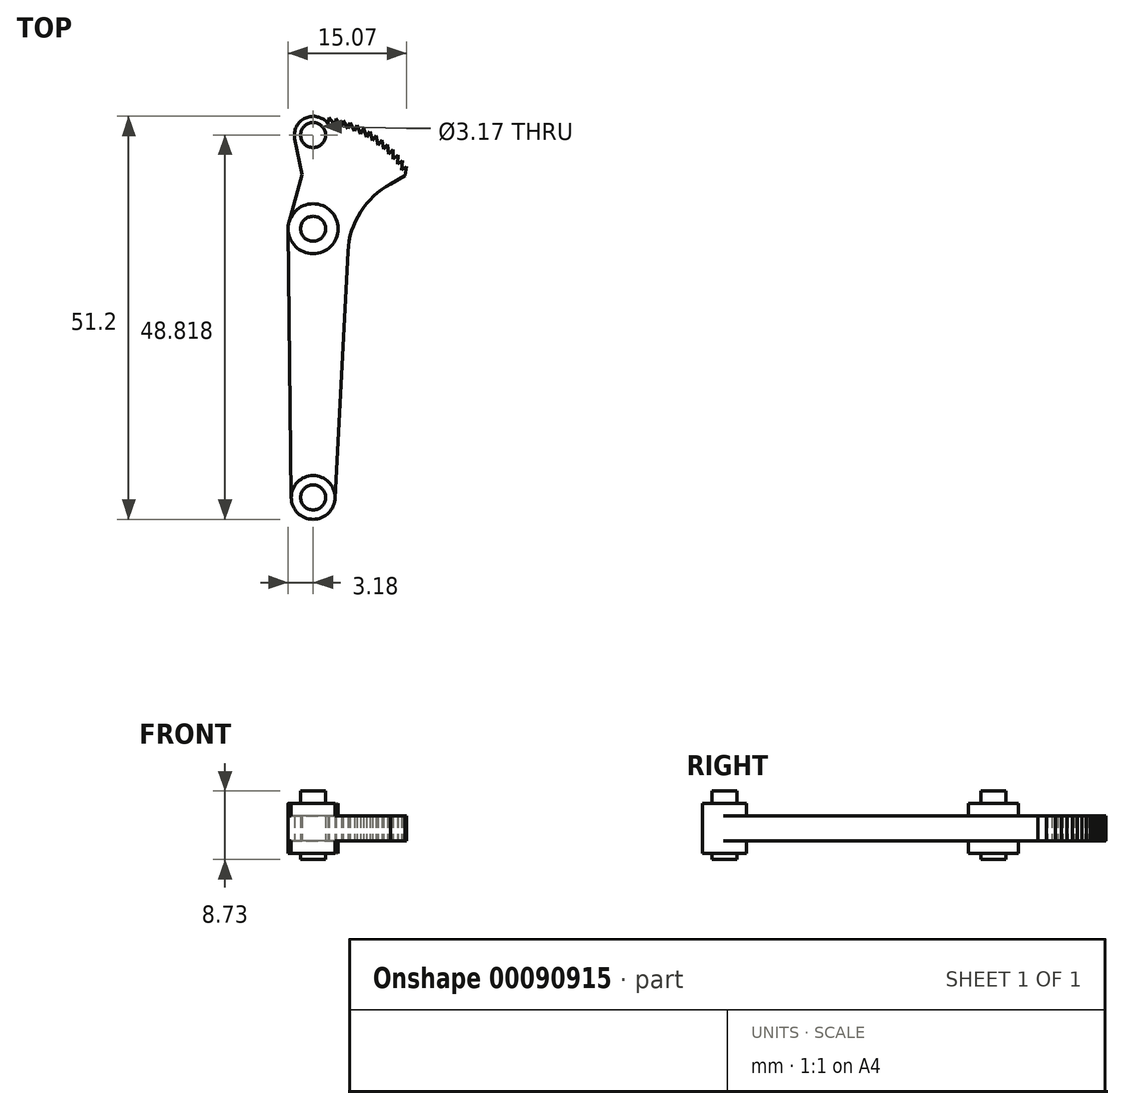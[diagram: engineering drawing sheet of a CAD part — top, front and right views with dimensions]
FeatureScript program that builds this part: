
annotation { "Feature Type Name" : "Feature", "Feature Type Description" : "" }
export const myFeature = defineFeature(function(context is Context, id is Id, definition is map)
    precondition{}
    {
        {
            var Q0;
            Q0=qCreatedBy(makeId("Top.planeOp"),FACE);
            var sketch = newSketch(context, id + "F0", { "sketchPlane" : qUnion([Q0])});
            skCircle(sketch, "E0", {"center": v(0, 0) * mm, "radius": 2.78 * mm});
            skCircle(sketch, "E1", {"center": v(0, 0) * mm, "radius": 1.59 * mm});
            skCircle(sketch, "E2", {"center": v(0, 34.13) * mm, "radius": 3.18 * mm});
            skCircle(sketch, "E3", {"center": v(0, 34.13) * mm, "radius": 1.59 * mm});
            skCircle(sketch, "E4", {"center": v(0, 46.04) * mm, "radius": 1.59 * mm});
            skLineSegment(sketch, "E5", {"start": v(0, 0) * mm, "end": v(0, 46.04) * mm, "construction": true});
            skArc(sketch, "E6", {"start": v(1.9, 47.48) * mm, "mid": v(-0.98, 48.2) * mm, "end": v(-2.33, 45.56) * mm});
            skLineSegment(sketch, "E7", {"start": v(2.77, -0.15) * mm, "end": v(4.42, 31.26) * mm});
            skArc(sketch, "E8.filletArc", {"start": v(9.85, 39.82) * mm, "mid": v(6.01, 36.25) * mm, "end": v(4.42, 31.26) * mm});
            skLineSegment(sketch, "E9", {"start": v(-2.78, -0.03) * mm, "end": v(-3.17, 34.1) * mm});
            skLineSegment(sketch, "E10", {"start": v(2.02, 48.27) * mm, "end": v(2.75, 47.33) * mm});
            skLineSegment(sketch, "E11.trimOffspring", {"start": v(1.9, 47.48) * mm, "end": v(2.02, 48.27) * mm});
            skLineSegment(sketch, "E12.trimOffspring", {"start": v(9.85, 39.82) * mm, "end": v(11.68, 40.87) * mm});
            skLineSegment(sketch, "E13.1.0", {"start": v(2.75, 47.33) * mm, "end": v(2.93, 48.11) * mm});
            skLineSegment(sketch, "E13.1.1", {"start": v(2.93, 48.11) * mm, "end": v(3.6, 47.12) * mm});
            skLineSegment(sketch, "E13.2.0", {"start": v(3.6, 47.12) * mm, "end": v(3.83, 47.9) * mm});
            skLineSegment(sketch, "E13.2.1", {"start": v(3.83, 47.9) * mm, "end": v(4.43, 46.86) * mm});
            skLineSegment(sketch, "E13.3.0", {"start": v(4.43, 46.86) * mm, "end": v(4.71, 47.62) * mm});
            skLineSegment(sketch, "E13.3.1", {"start": v(4.71, 47.62) * mm, "end": v(5.25, 46.55) * mm});
            skLineSegment(sketch, "E13.4.0", {"start": v(5.25, 46.55) * mm, "end": v(5.57, 47.29) * mm});
            skLineSegment(sketch, "E13.4.1", {"start": v(5.57, 47.29) * mm, "end": v(6.04, 46.18) * mm});
            skLineSegment(sketch, "E13.5.0", {"start": v(6.04, 46.18) * mm, "end": v(6.41, 46.9) * mm});
            skLineSegment(sketch, "E13.5.1", {"start": v(6.41, 46.9) * mm, "end": v(6.8, 45.77) * mm});
            skLineSegment(sketch, "E13.6.0", {"start": v(6.8, 45.77) * mm, "end": v(7.23, 46.46) * mm});
            skLineSegment(sketch, "E13.6.1", {"start": v(7.23, 46.46) * mm, "end": v(7.55, 45.3) * mm});
            skLineSegment(sketch, "E13.7.0", {"start": v(7.55, 45.3) * mm, "end": v(8, 45.96) * mm});
            skLineSegment(sketch, "E13.7.1", {"start": v(8, 45.96) * mm, "end": v(8.25, 44.8) * mm});
            skLineSegment(sketch, "E13.8.0", {"start": v(8.25, 44.8) * mm, "end": v(8.76, 45.42) * mm});
            skLineSegment(sketch, "E13.8.1", {"start": v(8.76, 45.42) * mm, "end": v(8.93, 44.24) * mm});
            skLineSegment(sketch, "E13.9.0", {"start": v(8.93, 44.24) * mm, "end": v(9.47, 44.83) * mm});
            skLineSegment(sketch, "E13.9.1", {"start": v(9.47, 44.83) * mm, "end": v(9.56, 43.64) * mm});
            skLineSegment(sketch, "E13.10.0", {"start": v(9.56, 43.64) * mm, "end": v(10.14, 44.2) * mm});
            skLineSegment(sketch, "E13.10.1", {"start": v(10.14, 44.2) * mm, "end": v(10.16, 43) * mm});
            skLineSegment(sketch, "E13.11.0", {"start": v(10.16, 43) * mm, "end": v(10.77, 43.52) * mm});
            skLineSegment(sketch, "E13.11.1", {"start": v(10.77, 43.52) * mm, "end": v(10.7, 42.32) * mm});
            skLineSegment(sketch, "E13.12.0", {"start": v(10.7, 42.32) * mm, "end": v(11.36, 42.8) * mm});
            skLineSegment(sketch, "E13.12.1", {"start": v(11.36, 42.8) * mm, "end": v(11.22, 41.61) * mm});
            skLineSegment(sketch, "E13.13.0", {"start": v(11.22, 41.61) * mm, "end": v(11.9, 42.05) * mm});
            skLineSegment(sketch, "E13.13.1", {"start": v(11.9, 42.05) * mm, "end": v(11.68, 40.87) * mm});
            skLineSegment(sketch, "E13.anchor1", {"start": v(0, 34.13) * mm, "end": v(1.9, 47.48) * mm, "construction": true});
            skLineSegment(sketch, "E14", {"start": v(0, 0) * mm, "end": v(23.83, 0) * mm, "construction": true});
            skLineSegment(sketch, "E15", {"start": v(-3.06, 34.98) * mm, "end": v(-1.4, 40.98) * mm});
            skLineSegment(sketch, "E16", {"start": v(-2.33, 45.56) * mm, "end": v(-1.4, 40.98) * mm});
            skLineSegment(sketch, "E17.trimOffspring", {"start": v(6.04, 46.18) * mm, "end": v(6.04, 46.18) * mm});
            skLineSegment(sketch, "E18.trimOffspring", {"start": v(5.25, 46.55) * mm, "end": v(5.25, 46.55) * mm});
            skSolve(sketch);
        }
        {
            var Q0;
            Q0=makeQuery(id+"F0.imprint","IMPRINT",FACE,{"disambiguationData":[TD([[makeQuery(id+"F0.imprint","IMPRINT",EDGE,{"derivedFrom":sQuery(id+"F0.wireOp",EDGE,"E4")}),-1.0]])]});
            extrude(context, id + "F1", {"entities" : qUnion([Q0]), "endBound" : BoundingType.SYMMETRIC, "depth" : 3.17 * mm});
        }
        {
            var Q0;
            Q0=makeQuery(id+"F0.imprint","IMPRINT",FACE,{"disambiguationData":[TD([[makeQuery(id+"F0.imprint","IMPRINT",EDGE,{"derivedFrom":sQuery(id+"F0.wireOp",EDGE,"E3")}),-1.0]])]});
            var Q1;
            Q1=makeQuery(id+"F0.imprint","IMPRINT",FACE,{"disambiguationData":[TD([[makeQuery(id+"F0.imprint","IMPRINT",EDGE,{"derivedFrom":sQuery(id+"F0.wireOp",EDGE,"E1")}),-1.0]])]});
            extrude(context, id + "F2", {"entities" : qUnion([Q0, Q1]), "operationType" : NewBodyOperationType.ADD, "endBound" : BoundingType.SYMMETRIC, "depth" : 6.35 * mm});
        }
        {
            var Q0;
            Q0=makeQuery(id+"F0.imprint","IMPRINT",FACE,{"disambiguationData":[TD([[makeQuery(id+"F0.imprint","IMPRINT",EDGE,{"derivedFrom":sQuery(id+"F0.wireOp",EDGE,"E3")}),1.0]])]});
            extrude(context, id + "F3", {"entities" : qUnion([Q0]), "operationType" : NewBodyOperationType.ADD, "depth" : 4.76 * mm});
        }
        {
            var Q0;
            Q0=makeQuery(id+"F0.imprint","IMPRINT",FACE,{"disambiguationData":[TD([[makeQuery(id+"F0.imprint","IMPRINT",EDGE,{"derivedFrom":sQuery(id+"F0.wireOp",EDGE,"E3")}),1.0]])]});
            extrude(context, id + "F4", {"entities" : qUnion([Q0]), "operationType" : NewBodyOperationType.ADD, "oppositeDirection" : true, "depth" : 3.97 * mm});
        }
        {
            var Q0;
            Q0=makeQuery(id+"F0.imprint","IMPRINT",FACE,{"disambiguationData":[TD([[makeQuery(id+"F0.imprint","IMPRINT",EDGE,{"derivedFrom":sQuery(id+"F0.wireOp",EDGE,"E1")}),1.0]])]});
            extrude(context, id + "F5", {"entities" : qUnion([Q0]), "operationType" : NewBodyOperationType.ADD, "depth" : 4.76 * mm});
        }
        {
            var Q0;
            Q0=makeQuery(id+"F0.imprint","IMPRINT",FACE,{"disambiguationData":[TD([[makeQuery(id+"F0.imprint","IMPRINT",EDGE,{"derivedFrom":sQuery(id+"F0.wireOp",EDGE,"E1")}),1.0]])]});
            extrude(context, id + "F6", {"entities" : qUnion([Q0]), "operationType" : NewBodyOperationType.ADD, "oppositeDirection" : true, "depth" : 3.97 * mm});
        }
    });
